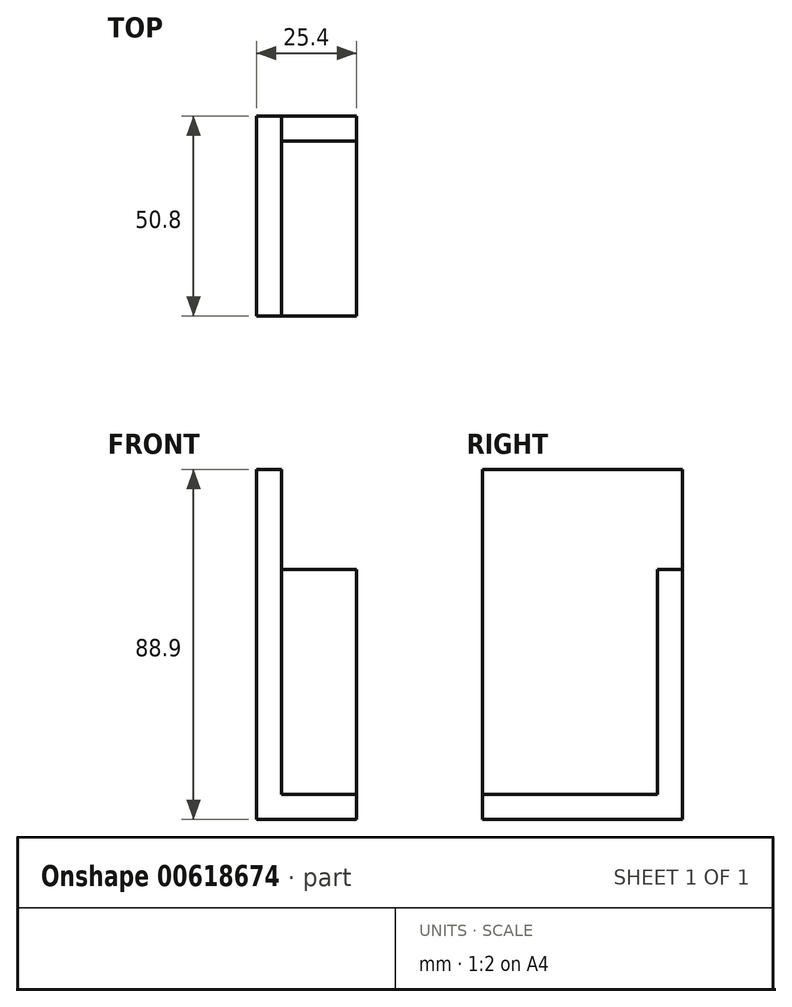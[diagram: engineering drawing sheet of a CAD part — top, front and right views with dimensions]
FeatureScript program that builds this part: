
annotation { "Feature Type Name" : "Feature", "Feature Type Description" : "" }
export const myFeature = defineFeature(function(context is Context, id is Id, definition is map)
    precondition{}
    {
        {
            var Q0;
            Q0=qCreatedBy(makeId("Front.planeOp"),FACE);
            var sketch = newSketch(context, id + "F0", { "sketchPlane" : qUnion([Q0])});
            skLineSegment(sketch, "E0.bottom", {"start": v(12.7, -44.45) * mm, "end": v(-12.7, -44.45) * mm});
            skLineSegment(sketch, "E0.top", {"start": v(12.7, 44.45) * mm, "end": v(-12.7, 44.45) * mm});
            skLineSegment(sketch, "E0.left", {"start": v(12.7, -44.45) * mm, "end": v(12.7, 44.45) * mm});
            skLineSegment(sketch, "E0.right", {"start": v(-12.7, -44.45) * mm, "end": v(-12.7, 44.45) * mm});
            skPoint(sketch, "E0.middle", {"position": v(0, 0) * mm});
            skSolve(sketch);
        }
        {
            var Q0;
            Q0=makeQuery(id+"F0.imprint","IMPRINT",FACE,{"disambiguationData":[TD([[makeQuery(id+"F0.imprint","IMPRINT",EDGE,{"derivedFrom":sQuery(id+"F0.wireOp",EDGE,"E0.bottom")}),-1.0]])]});
            extrude(context, id + "F1", {"entities" : qUnion([Q0]), "depth" : 50.8 * mm, "offsetDistance" : 25.4 * mm});
        }
        {
            var Q0;
            Q0=makeQuery(id+"F1.opExtrude","CAP_FACE",FACE,{"disambiguationData":[OSD([sQuery(id+"F0.wireOp",EDGE,"E0.bottom"),sQuery(id+"F0.wireOp",EDGE,"E0.top"),sQuery(id+"F0.wireOp",EDGE,"E0.left"),sQuery(id+"F0.wireOp",EDGE,"E0.right")])],"isStart":false});
            var sketch = newSketch(context, id + "F2", { "sketchPlane" : qUnion([Q0])});
            skLineSegment(sketch, "E1.bottom", {"start": v(-6.35, 44.45) * mm, "end": v(12.7, 44.45) * mm});
            skLineSegment(sketch, "E1.top", {"start": v(-6.35, -38.1) * mm, "end": v(12.7, -38.1) * mm});
            skLineSegment(sketch, "E1.left", {"start": v(-6.35, 44.45) * mm, "end": v(-6.35, -38.1) * mm});
            skLineSegment(sketch, "E1.right", {"start": v(12.7, 44.45) * mm, "end": v(12.7, -38.1) * mm});
            skSolve(sketch);
        }
        {
            var Q0;
            Q0=makeQuery(id+"F2.imprint","IMPRINT",FACE,{"disambiguationData":[TD([[makeQuery(id+"F2.imprint","IMPRINT",EDGE,{"derivedFrom":sQuery(id+"F2.wireOp",EDGE,"E1.bottom")}),1.0]])]});
            extrude(context, id + "F3", {"entities" : qUnion([Q0]), "operationType" : NewBodyOperationType.REMOVE, "oppositeDirection" : true, "depth" : 44.45 * mm, "offsetDistance" : 25.4 * mm});
        }
        {
            var Q0;
            Q0=makeQuery(id+"F1.opExtrude","SWEPT_FACE",FACE,{"disambiguationData":[OSD([sQuery(id+"F0.wireOp",EDGE,"E0.left")])]});
            var sketch = newSketch(context, id + "F4", { "sketchPlane" : qUnion([Q0])});
            skLineSegment(sketch, "E2.bottom", {"start": v(-6.35, -38.1) * mm, "end": v(0, -38.1) * mm});
            skLineSegment(sketch, "E2.top", {"start": v(-6.35, -44.45) * mm, "end": v(0, -44.45) * mm});
            skLineSegment(sketch, "E2.left", {"start": v(-6.35, -38.1) * mm, "end": v(-6.35, -44.45) * mm});
            skLineSegment(sketch, "E2.right", {"start": v(0, -38.1) * mm, "end": v(0, -44.45) * mm});
            skSolve(sketch);
        }
        {
            var Q0;
            Q0=makeQuery(id+"F4.imprint","IMPRINT",FACE,{"disambiguationData":[TD([[makeQuery(id+"F4.imprint","IMPRINT",EDGE,{"derivedFrom":sQuery(id+"F4.wireOp",EDGE,"E2.bottom")}),-1.0]])]});
            extrude(context, id + "F5", {"entities" : qUnion([Q0]), "operationType" : NewBodyOperationType.ADD, "oppositeDirection" : true, "depth" : 25.4 * mm, "offsetDistance" : 25.4 * mm});
        }
        {
            var Q0;
            Q0=makeQuery(id+"F1.opExtrude","CAP_FACE",FACE,{"disambiguationData":[OSD([sQuery(id+"F0.wireOp",EDGE,"E0.bottom"),sQuery(id+"F0.wireOp",EDGE,"E0.top"),sQuery(id+"F0.wireOp",EDGE,"E0.left"),sQuery(id+"F0.wireOp",EDGE,"E0.right")])],"isStart":true});
            var sketch = newSketch(context, id + "F6", { "sketchPlane" : qUnion([Q0])});
            skLineSegment(sketch, "E3.bottom", {"start": v(-12.7, 44.45) * mm, "end": v(6.35, 44.45) * mm});
            skLineSegment(sketch, "E3.top", {"start": v(-12.7, 19.05) * mm, "end": v(6.35, 19.05) * mm});
            skLineSegment(sketch, "E3.left", {"start": v(-12.7, 44.45) * mm, "end": v(-12.7, 19.05) * mm});
            skLineSegment(sketch, "E3.right", {"start": v(6.35, 44.45) * mm, "end": v(6.35, 19.05) * mm});
            skSolve(sketch);
        }
        {
            var Q0;
            Q0=makeQuery(id+"F6.imprint","IMPRINT",FACE,{"disambiguationData":[TD([[makeQuery(id+"F6.imprint","IMPRINT",EDGE,{"derivedFrom":sQuery(id+"F6.wireOp",EDGE,"E3.bottom")}),-1.0]])]});
            extrude(context, id + "F7", {"entities" : qUnion([Q0]), "operationType" : NewBodyOperationType.REMOVE, "oppositeDirection" : true, "depth" : 25.4 * mm, "offsetDistance" : 25.4 * mm});
        }
    });
